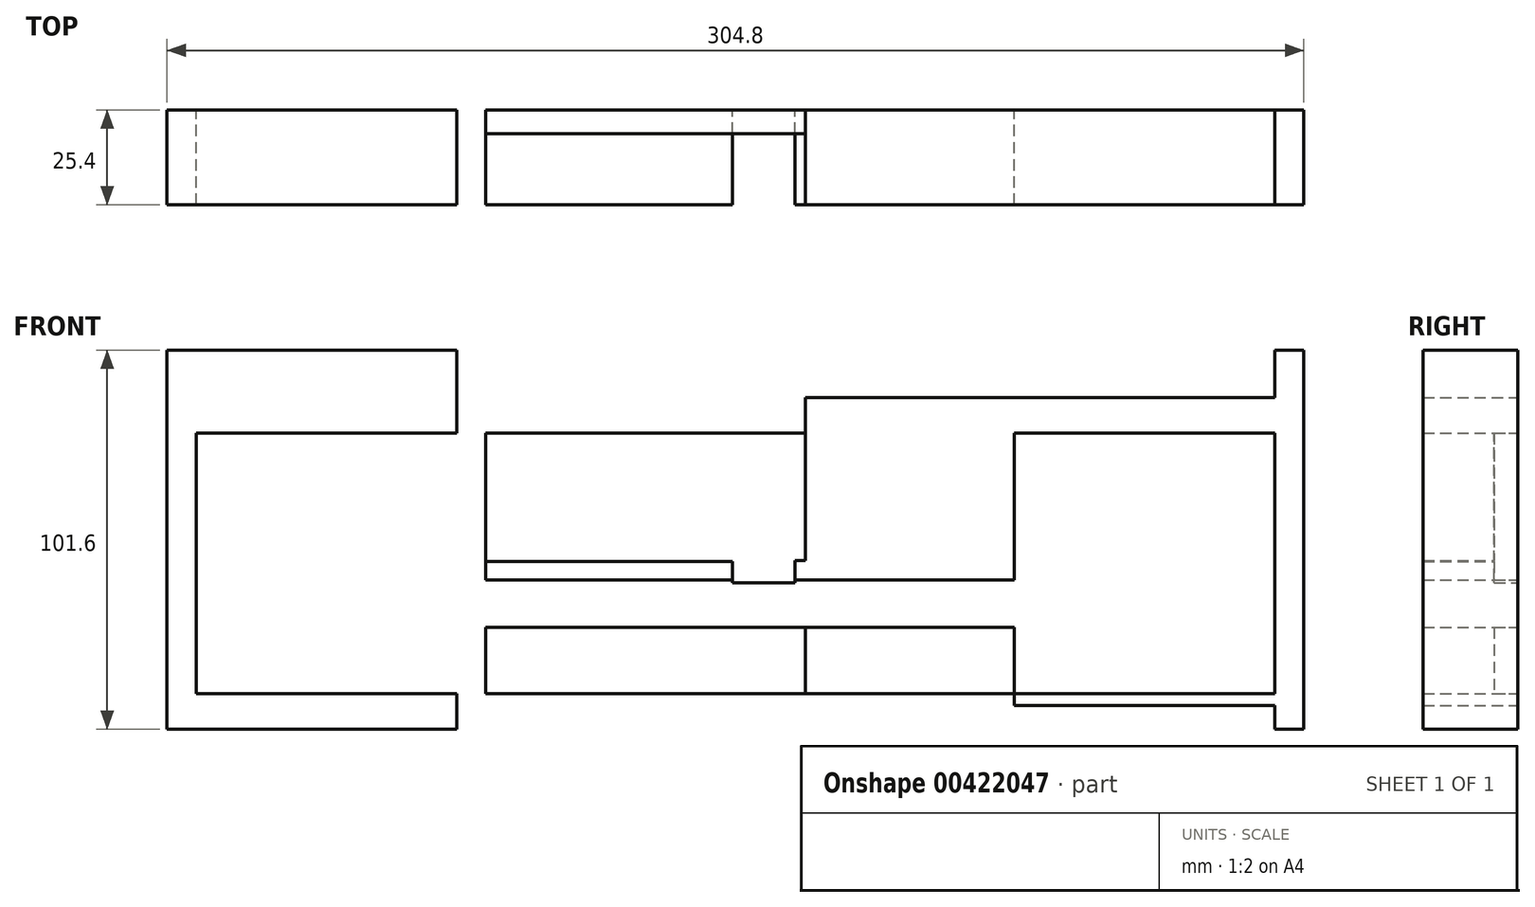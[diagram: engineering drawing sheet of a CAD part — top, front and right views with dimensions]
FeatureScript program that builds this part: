
annotation { "Feature Type Name" : "Feature", "Feature Type Description" : "" }
export const myFeature = defineFeature(function(context is Context, id is Id, definition is map)
    precondition{}
    {
        {
            var Q0;
            Q0=qCreatedBy(makeId("Front.planeOp"),FACE);
            var sketch = newSketch(context, id + "F0", { "sketchPlane" : qUnion([Q0])});
            skLineSegment(sketch, "E0.bottom", {"start": v(152.4, 59.41) * mm, "end": v(-152.4, 59.41) * mm});
            skLineSegment(sketch, "E0.top", {"start": v(152.4, -42.19) * mm, "end": v(-152.4, -42.19) * mm});
            skLineSegment(sketch, "E0.left", {"start": v(152.4, 59.41) * mm, "end": v(152.4, -42.19) * mm});
            skLineSegment(sketch, "E0.right", {"start": v(-152.4, 59.41) * mm, "end": v(-152.4, -42.19) * mm});
            skPoint(sketch, "E0.middle", {"position": v(0, 8.61) * mm});
            skLineSegment(sketch, "E1.bottom", {"start": v(-152.4, 59.41) * mm, "end": v(-144.58, 59.41) * mm});
            skLineSegment(sketch, "E1.top", {"start": v(-152.4, -42.19) * mm, "end": v(-144.58, -42.19) * mm});
            skLineSegment(sketch, "E1.right", {"start": v(-144.58, 59.41) * mm, "end": v(-144.58, -42.19) * mm});
            skLineSegment(sketch, "E2.bottom", {"start": v(152.4, 59.41) * mm, "end": v(144.58, 59.41) * mm});
            skLineSegment(sketch, "E2.top", {"start": v(152.4, -42.19) * mm, "end": v(144.58, -42.19) * mm});
            skLineSegment(sketch, "E2.right", {"start": v(144.58, 59.41) * mm, "end": v(144.58, -42.19) * mm});
            skLineSegment(sketch, "E3.bottom", {"start": v(-152.4, 59.41) * mm, "end": v(152.4, 59.41) * mm});
            skLineSegment(sketch, "E3.top", {"start": v(-152.4, 53.06) * mm, "end": v(152.4, 53.06) * mm});
            skLineSegment(sketch, "E3.left", {"start": v(-152.4, 59.41) * mm, "end": v(-152.4, 53.06) * mm});
            skLineSegment(sketch, "E3.right", {"start": v(152.4, 59.41) * mm, "end": v(152.4, 53.06) * mm});
            skLineSegment(sketch, "E4.bottom", {"start": v(-152.4, -42.19) * mm, "end": v(152.4, -42.19) * mm});
            skLineSegment(sketch, "E4.top", {"start": v(-152.4, -35.84) * mm, "end": v(152.4, -35.84) * mm});
            skLineSegment(sketch, "E4.left", {"start": v(-152.4, -42.19) * mm, "end": v(-152.4, -35.84) * mm});
            skLineSegment(sketch, "E4.right", {"start": v(152.4, -42.19) * mm, "end": v(152.4, -35.84) * mm});
            skLineSegment(sketch, "E5.bottom", {"start": v(-152.4, 59.41) * mm, "end": v(-74.73, 59.41) * mm});
            skLineSegment(sketch, "E5.top", {"start": v(-152.4, -42.19) * mm, "end": v(-74.73, -42.19) * mm});
            skLineSegment(sketch, "E5.right", {"start": v(-74.73, 59.41) * mm, "end": v(-74.73, -42.19) * mm});
            skLineSegment(sketch, "E6.bottom", {"start": v(152.4, 59.41) * mm, "end": v(74.73, 59.41) * mm});
            skLineSegment(sketch, "E6.top", {"start": v(152.4, -42.19) * mm, "end": v(74.73, -42.19) * mm});
            skLineSegment(sketch, "E6.right", {"start": v(74.73, 59.41) * mm, "end": v(74.73, -42.19) * mm});
            skLineSegment(sketch, "E7.bottom", {"start": v(74.73, -42.19) * mm, "end": v(-74.73, -42.19) * mm});
            skLineSegment(sketch, "E7.top", {"start": v(74.73, -14.88) * mm, "end": v(-74.73, -14.88) * mm});
            skLineSegment(sketch, "E7.left", {"start": v(74.73, -42.19) * mm, "end": v(74.73, -14.88) * mm});
            skLineSegment(sketch, "E7.right", {"start": v(-74.73, -42.19) * mm, "end": v(-74.73, -14.88) * mm});
            skLineSegment(sketch, "E8.bottom", {"start": v(-74.73, -14.88) * mm, "end": v(74.73, -14.88) * mm});
            skLineSegment(sketch, "E8.top", {"start": v(-74.73, -35.84) * mm, "end": v(74.73, -35.84) * mm});
            skLineSegment(sketch, "E8.left", {"start": v(-74.73, -14.88) * mm, "end": v(-74.73, -35.84) * mm});
            skLineSegment(sketch, "E8.right", {"start": v(74.73, -14.88) * mm, "end": v(74.73, -35.84) * mm});
            skLineSegment(sketch, "E9.top", {"start": v(-74.73, -2.18) * mm, "end": v(74.73, -2.18) * mm});
            skLineSegment(sketch, "E9.left", {"start": v(-74.73, -14.88) * mm, "end": v(-74.73, -2.18) * mm});
            skLineSegment(sketch, "E9.right", {"start": v(74.73, -14.88) * mm, "end": v(74.73, -2.18) * mm});
            skLineSegment(sketch, "E10.bottom", {"start": v(-74.73, -42.19) * mm, "end": v(-66.93, -42.19) * mm});
            skLineSegment(sketch, "E10.top", {"start": v(-74.73, 59.41) * mm, "end": v(-66.93, 59.41) * mm});
            skLineSegment(sketch, "E10.left", {"start": v(-74.73, -42.19) * mm, "end": v(-74.73, 59.41) * mm});
            skLineSegment(sketch, "E10.right", {"start": v(-66.93, -42.19) * mm, "end": v(-66.93, 59.41) * mm});
            skLineSegment(sketch, "E11.bottom", {"start": v(-66.93, 59.41) * mm, "end": v(18.8, 59.41) * mm});
            skLineSegment(sketch, "E11.top", {"start": v(-66.93, -42.19) * mm, "end": v(18.8, -42.19) * mm});
            skLineSegment(sketch, "E11.left", {"start": v(-66.93, 59.41) * mm, "end": v(-66.93, -42.19) * mm});
            skLineSegment(sketch, "E11.right", {"start": v(18.8, 59.41) * mm, "end": v(18.8, -42.19) * mm});
            skLineSegment(sketch, "E12.bottom", {"start": v(-66.93, 2.73) * mm, "end": v(-0.84, 2.73) * mm});
            skLineSegment(sketch, "E12.top", {"start": v(-66.93, -28.32) * mm, "end": v(-0.84, -28.32) * mm});
            skLineSegment(sketch, "E12.left", {"start": v(-66.93, 2.73) * mm, "end": v(-66.93, -28.32) * mm});
            skLineSegment(sketch, "E12.right", {"start": v(-0.84, 2.73) * mm, "end": v(-0.84, -28.32) * mm});
            skLineSegment(sketch, "E13.bottom", {"start": v(-0.84, -28.32) * mm, "end": v(15.93, -28.32) * mm});
            skLineSegment(sketch, "E13.top", {"start": v(-0.84, 3) * mm, "end": v(15.93, 3) * mm});
            skLineSegment(sketch, "E13.left", {"start": v(-0.84, -28.32) * mm, "end": v(-0.84, 3) * mm});
            skLineSegment(sketch, "E13.right", {"start": v(15.93, -28.32) * mm, "end": v(15.93, 3) * mm});
            skLineSegment(sketch, "E14.bottom", {"start": v(15.93, 3) * mm, "end": v(18.8, 3) * mm});
            skLineSegment(sketch, "E14.top", {"start": v(15.93, -28.32) * mm, "end": v(18.8, -28.32) * mm});
            skLineSegment(sketch, "E14.left", {"start": v(15.93, 3) * mm, "end": v(15.93, -28.32) * mm});
            skLineSegment(sketch, "E14.right", {"start": v(18.8, 3) * mm, "end": v(18.8, -28.32) * mm});
            skLineSegment(sketch, "E15.bottom", {"start": v(-0.84, -14.88) * mm, "end": v(15.93, -14.88) * mm});
            skLineSegment(sketch, "E15.top", {"start": v(-0.84, -2.95) * mm, "end": v(15.93, -2.95) * mm});
            skLineSegment(sketch, "E15.left", {"start": v(-0.84, -14.88) * mm, "end": v(-0.84, -2.95) * mm});
            skLineSegment(sketch, "E15.right", {"start": v(15.93, -14.88) * mm, "end": v(15.93, -2.95) * mm});
            skLineSegment(sketch, "E16.top", {"start": v(-152.4, -32.66) * mm, "end": v(152.4, -32.66) * mm});
            skLineSegment(sketch, "E16.left", {"start": v(-152.4, -42.19) * mm, "end": v(-152.4, -32.66) * mm});
            skLineSegment(sketch, "E16.right", {"start": v(152.4, -42.19) * mm, "end": v(152.4, -32.66) * mm});
            skLineSegment(sketch, "E17.top", {"start": v(-152.4, 49.89) * mm, "end": v(152.4, 49.89) * mm});
            skLineSegment(sketch, "E17.left", {"start": v(-152.4, 59.41) * mm, "end": v(-152.4, 49.89) * mm});
            skLineSegment(sketch, "E17.right", {"start": v(152.4, 59.41) * mm, "end": v(152.4, 49.89) * mm});
            skLineSegment(sketch, "E18.top", {"start": v(-152.4, 46.71) * mm, "end": v(152.4, 46.71) * mm});
            skLineSegment(sketch, "E18.left", {"start": v(-152.4, -42.19) * mm, "end": v(-152.4, 46.71) * mm});
            skLineSegment(sketch, "E18.right", {"start": v(152.4, -42.19) * mm, "end": v(152.4, 46.71) * mm});
            skLineSegment(sketch, "E19.top", {"start": v(-152.4, 37.19) * mm, "end": v(152.4, 37.19) * mm});
            skLineSegment(sketch, "E19.left", {"start": v(-152.4, 46.71) * mm, "end": v(-152.4, 37.19) * mm});
            skLineSegment(sketch, "E19.right", {"start": v(152.4, 46.71) * mm, "end": v(152.4, 37.19) * mm});
            skLineSegment(sketch, "E20.top", {"start": v(-152.4, 40.36) * mm, "end": v(152.4, 40.36) * mm});
            skLineSegment(sketch, "E20.left", {"start": v(-152.4, 46.71) * mm, "end": v(-152.4, 40.36) * mm});
            skLineSegment(sketch, "E20.right", {"start": v(152.4, 46.71) * mm, "end": v(152.4, 40.36) * mm});
            skSolve(sketch);
        }
        {
            var Q0;
            {var subQ0=sQuery(id+"F0.wireOp",EDGE,"E4.bottom");var subQ1=sQuery(id+"F0.wireOp",EDGE,"E2.right");var subQ2=makeQuery(id+"F0.imprint","INTERSECT",VERTEX,{"derivedFrom":[subQ1,subQ0]});Q0=makeQuery(id+"F0.imprint","IMPRINT",FACE,{"disambiguationData":[TD([[makeQuery(id+"F0.imprint","IMPRINT",EDGE,{"disambiguationData":[TD([[subQ2,1.0]])],"derivedFrom":subQ1}),1.0]])]});}
            var Q1;
            {var subQ5=sQuery(id+"F0.wireOp",EDGE,"E20.right");Q1=makeQuery(id+"F0.imprint","IMPRINT",FACE,{"disambiguationData":[TD([[makeQuery(id+"F0.imprint","IMPRINT",EDGE,{"derivedFrom":subQ5}),-1.0]])]});}
            var Q2;
            {var subQ5=sQuery(id+"F0.wireOp",EDGE,"E19.right");Q2=makeQuery(id+"F0.imprint","IMPRINT",FACE,{"disambiguationData":[TD([[makeQuery(id+"F0.imprint","IMPRINT",EDGE,{"derivedFrom":subQ5}),-1.0]])]});}
            var Q3;
            {var subQ0=sQuery(id+"F0.wireOp",EDGE,"E19.top");var subQ1=sQuery(id+"F0.wireOp",EDGE,"E2.right");var subQ2=makeQuery(id+"F0.imprint","INTERSECT",VERTEX,{"derivedFrom":[subQ1,subQ0]});Q3=makeQuery(id+"F0.imprint","IMPRINT",FACE,{"disambiguationData":[TD([[makeQuery(id+"F0.imprint","IMPRINT",EDGE,{"disambiguationData":[TD([[subQ2,-1.0]])],"derivedFrom":subQ1}),1.0]])]});}
            var Q4;
            {var subQ0=sQuery(id+"F0.wireOp",EDGE,"E16.top");var subQ1=sQuery(id+"F0.wireOp",EDGE,"E2.right");var subQ2=makeQuery(id+"F0.imprint","INTERSECT",VERTEX,{"derivedFrom":[subQ1,subQ0]});Q4=makeQuery(id+"F0.imprint","IMPRINT",FACE,{"disambiguationData":[TD([[makeQuery(id+"F0.imprint","IMPRINT",EDGE,{"disambiguationData":[TD([[subQ2,-1.0]])],"derivedFrom":subQ1}),1.0]])]});}
            var Q5;
            {var subQ0=sQuery(id+"F0.wireOp",EDGE,"E4.bottom");var subQ1=sQuery(id+"F0.wireOp",EDGE,"E1.right");var subQ2=makeQuery(id+"F0.imprint","INTERSECT",VERTEX,{"derivedFrom":[subQ1,subQ0]});Q5=makeQuery(id+"F0.imprint","IMPRINT",FACE,{"disambiguationData":[TD([[makeQuery(id+"F0.imprint","IMPRINT",EDGE,{"disambiguationData":[TD([[subQ2,1.0]])],"derivedFrom":subQ1}),-1.0]])]});}
            var Q6;
            {var subQ5=sQuery(id+"F0.wireOp",EDGE,"E20.left");Q6=makeQuery(id+"F0.imprint","IMPRINT",FACE,{"disambiguationData":[TD([[makeQuery(id+"F0.imprint","IMPRINT",EDGE,{"derivedFrom":subQ5}),1.0]])]});}
            var Q7;
            {var subQ5=sQuery(id+"F0.wireOp",EDGE,"E19.left");Q7=makeQuery(id+"F0.imprint","IMPRINT",FACE,{"disambiguationData":[TD([[makeQuery(id+"F0.imprint","IMPRINT",EDGE,{"derivedFrom":subQ5}),1.0]])]});}
            var Q8;
            {var subQ0=sQuery(id+"F0.wireOp",EDGE,"E19.top");var subQ1=sQuery(id+"F0.wireOp",EDGE,"E1.right");var subQ2=makeQuery(id+"F0.imprint","INTERSECT",VERTEX,{"derivedFrom":[subQ1,subQ0]});Q8=makeQuery(id+"F0.imprint","IMPRINT",FACE,{"disambiguationData":[TD([[makeQuery(id+"F0.imprint","IMPRINT",EDGE,{"disambiguationData":[TD([[subQ2,-1.0]])],"derivedFrom":subQ1}),-1.0]])]});}
            var Q9;
            {var subQ0=sQuery(id+"F0.wireOp",EDGE,"E16.top");var subQ1=sQuery(id+"F0.wireOp",EDGE,"E1.right");var subQ2=makeQuery(id+"F0.imprint","INTERSECT",VERTEX,{"derivedFrom":[subQ1,subQ0]});Q9=makeQuery(id+"F0.imprint","IMPRINT",FACE,{"disambiguationData":[TD([[makeQuery(id+"F0.imprint","IMPRINT",EDGE,{"disambiguationData":[TD([[subQ2,-1.0]])],"derivedFrom":subQ1}),-1.0]])]});}
            var Q10;
            {var subQ0=sQuery(id+"F0.wireOp",EDGE,"E16.top");var subQ1=sQuery(id+"F0.wireOp",EDGE,"E1.right");var subQ2=makeQuery(id+"F0.imprint","INTERSECT",VERTEX,{"derivedFrom":[subQ1,subQ0]});Q10=makeQuery(id+"F0.imprint","IMPRINT",FACE,{"disambiguationData":[TD([[makeQuery(id+"F0.imprint","IMPRINT",EDGE,{"disambiguationData":[TD([[subQ2,-1.0]])],"derivedFrom":subQ1}),-1.0]])]});}
            var Q11;
            {var subQ0=sQuery(id+"F0.wireOp",EDGE,"E4.bottom");var subQ1=sQuery(id+"F0.wireOp",EDGE,"E2.right");var subQ2=makeQuery(id+"F0.imprint","INTERSECT",VERTEX,{"derivedFrom":[subQ1,subQ0]});Q11=makeQuery(id+"F0.imprint","IMPRINT",FACE,{"disambiguationData":[TD([[makeQuery(id+"F0.imprint","IMPRINT",EDGE,{"disambiguationData":[TD([[subQ2,1.0]])],"derivedFrom":subQ1}),1.0]])]});}
            var Q12;
            {var subQ5=sQuery(id+"F0.wireOp",EDGE,"E20.right");Q12=makeQuery(id+"F0.imprint","IMPRINT",FACE,{"disambiguationData":[TD([[makeQuery(id+"F0.imprint","IMPRINT",EDGE,{"derivedFrom":subQ5}),-1.0]])]});}
            var Q13;
            {var subQ5=sQuery(id+"F0.wireOp",EDGE,"E19.right");Q13=makeQuery(id+"F0.imprint","IMPRINT",FACE,{"disambiguationData":[TD([[makeQuery(id+"F0.imprint","IMPRINT",EDGE,{"derivedFrom":subQ5}),-1.0]])]});}
            var Q14;
            {var subQ0=sQuery(id+"F0.wireOp",EDGE,"E19.top");var subQ1=sQuery(id+"F0.wireOp",EDGE,"E2.right");var subQ2=makeQuery(id+"F0.imprint","INTERSECT",VERTEX,{"derivedFrom":[subQ1,subQ0]});Q14=makeQuery(id+"F0.imprint","IMPRINT",FACE,{"disambiguationData":[TD([[makeQuery(id+"F0.imprint","IMPRINT",EDGE,{"disambiguationData":[TD([[subQ2,-1.0]])],"derivedFrom":subQ1}),1.0]])]});}
            var Q15;
            {var subQ0=sQuery(id+"F0.wireOp",EDGE,"E16.top");var subQ1=sQuery(id+"F0.wireOp",EDGE,"E2.right");var subQ2=makeQuery(id+"F0.imprint","INTERSECT",VERTEX,{"derivedFrom":[subQ1,subQ0]});Q15=makeQuery(id+"F0.imprint","IMPRINT",FACE,{"disambiguationData":[TD([[makeQuery(id+"F0.imprint","IMPRINT",EDGE,{"disambiguationData":[TD([[subQ2,-1.0]])],"derivedFrom":subQ1}),1.0]])]});}
            var Q16;
            {var subQ0=sQuery(id+"F0.wireOp",EDGE,"E16.top");var subQ1=sQuery(id+"F0.wireOp",EDGE,"E2.right");var subQ2=makeQuery(id+"F0.imprint","INTERSECT",VERTEX,{"derivedFrom":[subQ1,subQ0]});Q16=makeQuery(id+"F0.imprint","IMPRINT",FACE,{"disambiguationData":[TD([[makeQuery(id+"F0.imprint","IMPRINT",EDGE,{"disambiguationData":[TD([[subQ2,-1.0]])],"derivedFrom":subQ1}),1.0]])]});}
            var Q17;
            {var subQ5=sQuery(id+"F0.wireOp",EDGE,"E7.left");Q17=makeQuery(id+"F0.imprint","IMPRINT",FACE,{"disambiguationData":[TD([[makeQuery(id+"F0.imprint","IMPRINT",EDGE,{"derivedFrom":subQ5}),-1.0]])]});}
            var Q18;
            {var subQ0=sQuery(id+"F0.wireOp",EDGE,"E16.top");var subQ1=sQuery(id+"F0.wireOp",EDGE,"E2.right");var subQ2=makeQuery(id+"F0.imprint","INTERSECT",VERTEX,{"derivedFrom":[subQ1,subQ0]});Q18=makeQuery(id+"F0.imprint","IMPRINT",FACE,{"disambiguationData":[TD([[makeQuery(id+"F0.imprint","IMPRINT",EDGE,{"disambiguationData":[TD([[subQ2,-1.0]])],"derivedFrom":subQ1}),-1.0]])]});}
            var Q19;
            {var subQ1=sQuery(id+"F0.wireOp",EDGE,"E8.top");var subQ3=sQuery(id+"F0.wireOp",EDGE,"E11.right");var subQ4=makeQuery(id+"F0.imprint","INTERSECT",VERTEX,{"derivedFrom":[subQ1,subQ3]});Q19=makeQuery(id+"F0.imprint","IMPRINT",FACE,{"disambiguationData":[TD([[makeQuery(id+"F0.imprint","IMPRINT",EDGE,{"disambiguationData":[TD([[subQ4,1.0]])],"derivedFrom":subQ3}),1.0]])]});}
            var Q20;
            {var subQ0=sQuery(id+"F0.wireOp",EDGE,"E7.left");Q20=makeQuery(id+"F0.imprint","IMPRINT",FACE,{"disambiguationData":[TD([[makeQuery(id+"F0.imprint","IMPRINT",EDGE,{"derivedFrom":subQ0}),1.0]])]});}
            var Q21;
            {var subQ0=sQuery(id+"F0.wireOp",EDGE,"E11.left");var subQ1=sQuery(id+"F0.wireOp",EDGE,"E8.top");var subQ2=makeQuery(id+"F0.imprint","INTERSECT",VERTEX,{"derivedFrom":[subQ1,subQ0]});Q21=makeQuery(id+"F0.imprint","IMPRINT",FACE,{"disambiguationData":[TD([[makeQuery(id+"F0.imprint","IMPRINT",EDGE,{"disambiguationData":[TD([[subQ2,-1.0]])],"derivedFrom":subQ1}),-1.0]])]});}
            var Q22;
            {var subQ3=sQuery(id+"F0.wireOp",EDGE,"E11.left");var subQ5=sQuery(id+"F0.wireOp",EDGE,"E4.bottom");var subQ7=makeQuery(id+"F0.imprint","INTERSECT",VERTEX,{"derivedFrom":[subQ3,subQ5]});Q22=makeQuery(id+"F0.imprint","IMPRINT",FACE,{"disambiguationData":[TD([[makeQuery(id+"F0.imprint","IMPRINT",EDGE,{"disambiguationData":[TD([[subQ7,1.0]])],"derivedFrom":subQ3}),-1.0]])]});}
            var Q23;
            {var subQ1=sQuery(id+"F0.wireOp",EDGE,"E8.top");var subQ3=sQuery(id+"F0.wireOp",EDGE,"E11.left");var subQ4=makeQuery(id+"F0.imprint","INTERSECT",VERTEX,{"derivedFrom":[subQ1,subQ3]});Q23=makeQuery(id+"F0.imprint","IMPRINT",FACE,{"disambiguationData":[TD([[makeQuery(id+"F0.imprint","IMPRINT",EDGE,{"disambiguationData":[TD([[subQ4,1.0]])],"derivedFrom":subQ3}),-1.0]])]});}
            var Q24;
            {var subQ0=sQuery(id+"F0.wireOp",EDGE,"E19.top");var subQ1=sQuery(id+"F0.wireOp",EDGE,"E10.left");var subQ2=makeQuery(id+"F0.imprint","INTERSECT",VERTEX,{"derivedFrom":[subQ1,subQ0]});Q24=makeQuery(id+"F0.imprint","IMPRINT",FACE,{"disambiguationData":[TD([[makeQuery(id+"F0.imprint","IMPRINT",EDGE,{"disambiguationData":[TD([[subQ2,-1.0]])],"derivedFrom":subQ1}),-1.0]])]});}
            var Q25;
            {var subQ0=sQuery(id+"F0.wireOp",EDGE,"E20.top");var subQ1=sQuery(id+"F0.wireOp",EDGE,"E10.left");var subQ2=makeQuery(id+"F0.imprint","INTERSECT",VERTEX,{"derivedFrom":[subQ1,subQ0]});Q25=makeQuery(id+"F0.imprint","IMPRINT",FACE,{"disambiguationData":[TD([[makeQuery(id+"F0.imprint","IMPRINT",EDGE,{"disambiguationData":[TD([[subQ2,-1.0]])],"derivedFrom":subQ1}),-1.0]])]});}
            var Q26;
            {var subQ1=sQuery(id+"F0.wireOp",EDGE,"E8.top");var subQ3=sQuery(id+"F0.wireOp",EDGE,"E11.left");var subQ4=makeQuery(id+"F0.imprint","INTERSECT",VERTEX,{"derivedFrom":[subQ1,subQ3]});Q26=makeQuery(id+"F0.imprint","IMPRINT",FACE,{"disambiguationData":[TD([[makeQuery(id+"F0.imprint","IMPRINT",EDGE,{"disambiguationData":[TD([[subQ4,1.0]])],"derivedFrom":subQ3}),-1.0]])]});}
            var Q27;
            {var subQ0=sQuery(id+"F0.wireOp",EDGE,"E4.bottom");var subQ1=sQuery(id+"F0.wireOp",EDGE,"E1.right");var subQ2=makeQuery(id+"F0.imprint","INTERSECT",VERTEX,{"derivedFrom":[subQ1,subQ0]});Q27=makeQuery(id+"F0.imprint","IMPRINT",FACE,{"disambiguationData":[TD([[makeQuery(id+"F0.imprint","IMPRINT",EDGE,{"disambiguationData":[TD([[subQ2,1.0]])],"derivedFrom":subQ1}),1.0]])]});}
            var Q28;
            {var subQ0=sQuery(id+"F0.wireOp",EDGE,"E18.top");var subQ1=sQuery(id+"F0.wireOp",EDGE,"E1.right");var subQ2=makeQuery(id+"F0.imprint","INTERSECT",VERTEX,{"derivedFrom":[subQ1,subQ0]});Q28=makeQuery(id+"F0.imprint","IMPRINT",FACE,{"disambiguationData":[TD([[makeQuery(id+"F0.imprint","IMPRINT",EDGE,{"disambiguationData":[TD([[subQ2,-1.0]])],"derivedFrom":subQ1}),1.0]])]});}
            var Q29;
            {var subQ0=sQuery(id+"F0.wireOp",EDGE,"E20.top");var subQ1=sQuery(id+"F0.wireOp",EDGE,"E1.right");var subQ2=makeQuery(id+"F0.imprint","INTERSECT",VERTEX,{"derivedFrom":[subQ1,subQ0]});Q29=makeQuery(id+"F0.imprint","IMPRINT",FACE,{"disambiguationData":[TD([[makeQuery(id+"F0.imprint","IMPRINT",EDGE,{"disambiguationData":[TD([[subQ2,-1.0]])],"derivedFrom":subQ1}),1.0]])]});}
            var Q30;
            {var subQ0=sQuery(id+"F0.wireOp",EDGE,"E16.top");var subQ1=sQuery(id+"F0.wireOp",EDGE,"E1.right");var subQ2=makeQuery(id+"F0.imprint","INTERSECT",VERTEX,{"derivedFrom":[subQ1,subQ0]});Q30=makeQuery(id+"F0.imprint","IMPRINT",FACE,{"disambiguationData":[TD([[makeQuery(id+"F0.imprint","IMPRINT",EDGE,{"disambiguationData":[TD([[subQ2,-1.0]])],"derivedFrom":subQ1}),1.0]])]});}
            var Q31;
            {var subQ0=sQuery(id+"F0.wireOp",EDGE,"E16.top");var subQ1=sQuery(id+"F0.wireOp",EDGE,"E1.right");var subQ2=makeQuery(id+"F0.imprint","INTERSECT",VERTEX,{"derivedFrom":[subQ1,subQ0]});Q31=makeQuery(id+"F0.imprint","IMPRINT",FACE,{"disambiguationData":[TD([[makeQuery(id+"F0.imprint","IMPRINT",EDGE,{"disambiguationData":[TD([[subQ2,-1.0]])],"derivedFrom":subQ1}),1.0]])]});}
            var Q32;
            {var subQ5=sQuery(id+"F0.wireOp",EDGE,"E16.top");var subQ7=sQuery(id+"F0.wireOp",EDGE,"E8.right");var subQ9=makeQuery(id+"F0.imprint","INTERSECT",VERTEX,{"derivedFrom":[subQ7,subQ5]});Q32=makeQuery(id+"F0.imprint","IMPRINT",FACE,{"disambiguationData":[TD([[makeQuery(id+"F0.imprint","IMPRINT",EDGE,{"disambiguationData":[TD([[subQ9,1.0]])],"derivedFrom":subQ5}),1.0]])]});}
            var Q33;
            {var subQ0=sQuery(id+"F0.wireOp",EDGE,"E9.right");Q33=makeQuery(id+"F0.imprint","IMPRINT",FACE,{"disambiguationData":[TD([[makeQuery(id+"F0.imprint","IMPRINT",EDGE,{"derivedFrom":subQ0}),1.0]])]});}
            var Q34;
            {var subQ5=sQuery(id+"F0.wireOp",EDGE,"E8.bottom");var subQ7=sQuery(id+"F0.wireOp",EDGE,"E10.left");var subQ8=makeQuery(id+"F0.imprint","INTERSECT",VERTEX,{"derivedFrom":[subQ5,subQ7]});Q34=makeQuery(id+"F0.imprint","IMPRINT",FACE,{"disambiguationData":[TD([[makeQuery(id+"F0.imprint","IMPRINT",EDGE,{"disambiguationData":[TD([[subQ8,-1.0]])],"derivedFrom":subQ5}),-1.0]])]});}
            var Q35;
            {var subQ0=sQuery(id+"F0.wireOp",EDGE,"E10.left");var subQ1=sQuery(id+"F0.wireOp",EDGE,"E8.bottom");var subQ2=makeQuery(id+"F0.imprint","INTERSECT",VERTEX,{"derivedFrom":[subQ1,subQ0]});Q35=makeQuery(id+"F0.imprint","IMPRINT",FACE,{"disambiguationData":[TD([[makeQuery(id+"F0.imprint","IMPRINT",EDGE,{"disambiguationData":[TD([[subQ2,-1.0]])],"derivedFrom":subQ1}),1.0]])]});}
            var Q36;
            {var subQ3=sQuery(id+"F0.wireOp",EDGE,"E9.top");var subQ7=sQuery(id+"F0.wireOp",EDGE,"E10.left");var subQ8=makeQuery(id+"F0.imprint","INTERSECT",VERTEX,{"derivedFrom":[subQ3,subQ7]});Q36=makeQuery(id+"F0.imprint","IMPRINT",FACE,{"disambiguationData":[TD([[makeQuery(id+"F0.imprint","IMPRINT",EDGE,{"disambiguationData":[TD([[subQ8,-1.0]])],"derivedFrom":subQ3}),1.0]])]});}
            var Q37;
            {var subQ5=sQuery(id+"F0.wireOp",EDGE,"E19.top");var subQ7=sQuery(id+"F0.wireOp",EDGE,"E6.right");var subQ9=makeQuery(id+"F0.imprint","INTERSECT",VERTEX,{"derivedFrom":[subQ7,subQ5]});Q37=makeQuery(id+"F0.imprint","IMPRINT",FACE,{"disambiguationData":[TD([[makeQuery(id+"F0.imprint","IMPRINT",EDGE,{"disambiguationData":[TD([[subQ9,1.0]])],"derivedFrom":subQ5}),-1.0]])]});}
            var Q38;
            {var subQ0=sQuery(id+"F0.wireOp",EDGE,"E18.top");var subQ1=sQuery(id+"F0.wireOp",EDGE,"E6.right");var subQ2=makeQuery(id+"F0.imprint","INTERSECT",VERTEX,{"derivedFrom":[subQ1,subQ0]});Q38=makeQuery(id+"F0.imprint","IMPRINT",FACE,{"disambiguationData":[TD([[makeQuery(id+"F0.imprint","IMPRINT",EDGE,{"disambiguationData":[TD([[subQ2,-1.0]])],"derivedFrom":subQ1}),-1.0]])]});}
            var Q39;
            {var subQ0=sQuery(id+"F0.wireOp",EDGE,"E20.top");var subQ1=sQuery(id+"F0.wireOp",EDGE,"E6.right");var subQ2=makeQuery(id+"F0.imprint","INTERSECT",VERTEX,{"derivedFrom":[subQ1,subQ0]});Q39=makeQuery(id+"F0.imprint","IMPRINT",FACE,{"disambiguationData":[TD([[makeQuery(id+"F0.imprint","IMPRINT",EDGE,{"disambiguationData":[TD([[subQ2,-1.0]])],"derivedFrom":subQ1}),-1.0]])]});}
            var Q40;
            {var subQ0=sQuery(id+"F0.wireOp",EDGE,"E20.top");var subQ1=sQuery(id+"F0.wireOp",EDGE,"E2.right");var subQ2=makeQuery(id+"F0.imprint","INTERSECT",VERTEX,{"derivedFrom":[subQ1,subQ0]});Q40=makeQuery(id+"F0.imprint","IMPRINT",FACE,{"disambiguationData":[TD([[makeQuery(id+"F0.imprint","IMPRINT",EDGE,{"disambiguationData":[TD([[subQ2,-1.0]])],"derivedFrom":subQ1}),-1.0]])]});}
            var Q41;
            {var subQ0=sQuery(id+"F0.wireOp",EDGE,"E18.top");var subQ1=sQuery(id+"F0.wireOp",EDGE,"E2.right");var subQ2=makeQuery(id+"F0.imprint","INTERSECT",VERTEX,{"derivedFrom":[subQ1,subQ0]});Q41=makeQuery(id+"F0.imprint","IMPRINT",FACE,{"disambiguationData":[TD([[makeQuery(id+"F0.imprint","IMPRINT",EDGE,{"disambiguationData":[TD([[subQ2,-1.0]])],"derivedFrom":subQ1}),-1.0]])]});}
            extrude(context, id + "F1", {"entities" : qUnion([Q0, Q1, Q2, Q3, Q4, Q5, Q6, Q7, Q8, Q9, Q10, Q11, Q12, Q13, Q14, Q15, Q16, Q17, Q18, Q19, Q20, Q21, Q22, Q23, Q24, Q25, Q26, Q27, Q28, Q29, Q30, Q31, Q32, Q33, Q34, Q35, Q36, Q37, Q38, Q39, Q40, Q41]), "depth" : 25.4 * mm});
        }
        {
            var Q0;
            {var subQ5=sQuery(id+"F0.wireOp",EDGE,"E15.top");Q0=makeQuery(id+"F0.imprint","IMPRINT",FACE,{"disambiguationData":[TD([[makeQuery(id+"F0.imprint","IMPRINT",EDGE,{"derivedFrom":subQ5}),1.0]])]});}
            var Q1;
            {var subQ0=sQuery(id+"F0.wireOp",EDGE,"E13.bottom");Q1=makeQuery(id+"F0.imprint","IMPRINT",FACE,{"disambiguationData":[TD([[makeQuery(id+"F0.imprint","IMPRINT",EDGE,{"derivedFrom":subQ0}),1.0]])]});}
            var Q2;
            {var subQ4=sQuery(id+"F0.wireOp",EDGE,"E12.top");Q2=makeQuery(id+"F0.imprint","IMPRINT",FACE,{"disambiguationData":[TD([[makeQuery(id+"F0.imprint","IMPRINT",EDGE,{"derivedFrom":subQ4}),-1.0]])]});}
            var Q3;
            {var subQ0=sQuery(id+"F0.wireOp",EDGE,"E11.left");var subQ1=sQuery(id+"F0.wireOp",EDGE,"E8.top");var subQ2=makeQuery(id+"F0.imprint","INTERSECT",VERTEX,{"derivedFrom":[subQ1,subQ0]});Q3=makeQuery(id+"F0.imprint","IMPRINT",FACE,{"disambiguationData":[TD([[makeQuery(id+"F0.imprint","IMPRINT",EDGE,{"disambiguationData":[TD([[subQ2,-1.0]])],"derivedFrom":subQ1}),1.0]])]});}
            var Q4;
            {var subQ5=sQuery(id+"F0.wireOp",EDGE,"E12.top");Q4=makeQuery(id+"F0.imprint","IMPRINT",FACE,{"disambiguationData":[TD([[makeQuery(id+"F0.imprint","IMPRINT",EDGE,{"derivedFrom":subQ5}),1.0]])]});}
            var Q5;
            {var subQ5=sQuery(id+"F0.wireOp",EDGE,"E14.top");Q5=makeQuery(id+"F0.imprint","IMPRINT",FACE,{"disambiguationData":[TD([[makeQuery(id+"F0.imprint","IMPRINT",EDGE,{"derivedFrom":subQ5}),1.0]])]});}
            var Q6;
            {var subQ5=sQuery(id+"F0.wireOp",EDGE,"E15.right");Q6=makeQuery(id+"F0.imprint","IMPRINT",FACE,{"disambiguationData":[TD([[makeQuery(id+"F0.imprint","IMPRINT",EDGE,{"derivedFrom":subQ5}),-1.0]])]});}
            var Q7;
            {var subQ0=sQuery(id+"F0.wireOp",EDGE,"E15.left");Q7=makeQuery(id+"F0.imprint","IMPRINT",FACE,{"disambiguationData":[TD([[makeQuery(id+"F0.imprint","IMPRINT",EDGE,{"derivedFrom":subQ0}),1.0]])]});}
            var Q8;
            {var subQ5=sQuery(id+"F0.wireOp",EDGE,"E12.bottom");Q8=makeQuery(id+"F0.imprint","IMPRINT",FACE,{"disambiguationData":[TD([[makeQuery(id+"F0.imprint","IMPRINT",EDGE,{"derivedFrom":subQ5}),-1.0]])]});}
            var Q9;
            {var subQ2=sQuery(id+"F0.wireOp",EDGE,"E13.top");Q9=makeQuery(id+"F0.imprint","IMPRINT",FACE,{"disambiguationData":[TD([[makeQuery(id+"F0.imprint","IMPRINT",EDGE,{"derivedFrom":subQ2}),-1.0]])]});}
            var Q10;
            {var subQ5=sQuery(id+"F0.wireOp",EDGE,"E14.bottom");Q10=makeQuery(id+"F0.imprint","IMPRINT",FACE,{"disambiguationData":[TD([[makeQuery(id+"F0.imprint","IMPRINT",EDGE,{"derivedFrom":subQ5}),-1.0]])]});}
            var Q11;
            {var subQ7=sQuery(id+"F0.wireOp",EDGE,"E12.bottom");Q11=makeQuery(id+"F0.imprint","IMPRINT",FACE,{"disambiguationData":[TD([[makeQuery(id+"F0.imprint","IMPRINT",EDGE,{"derivedFrom":subQ7}),1.0]])]});}
            var Q12;
            {var subQ0=sQuery(id+"F0.wireOp",EDGE,"E20.top");var subQ1=sQuery(id+"F0.wireOp",EDGE,"E11.left");var subQ2=makeQuery(id+"F0.imprint","INTERSECT",VERTEX,{"derivedFrom":[subQ1,subQ0]});Q12=makeQuery(id+"F0.imprint","IMPRINT",FACE,{"disambiguationData":[TD([[makeQuery(id+"F0.imprint","IMPRINT",EDGE,{"disambiguationData":[TD([[subQ2,-1.0]])],"derivedFrom":subQ1}),1.0]])]});}
            var Q13;
            {var subQ0=sQuery(id+"F0.wireOp",EDGE,"E18.top");var subQ1=sQuery(id+"F0.wireOp",EDGE,"E11.left");var subQ2=makeQuery(id+"F0.imprint","INTERSECT",VERTEX,{"derivedFrom":[subQ1,subQ0]});Q13=makeQuery(id+"F0.imprint","IMPRINT",FACE,{"disambiguationData":[TD([[makeQuery(id+"F0.imprint","IMPRINT",EDGE,{"disambiguationData":[TD([[subQ2,-1.0]])],"derivedFrom":subQ1}),1.0]])]});}
            extrude(context, id + "F2", {"entities" : qUnion([Q0, Q1, Q2, Q3, Q4, Q5, Q6, Q7, Q8, Q9, Q10, Q11, Q12, Q13]), "operationType" : NewBodyOperationType.ADD, "depth" : 6.35 * mm});
        }
    });
